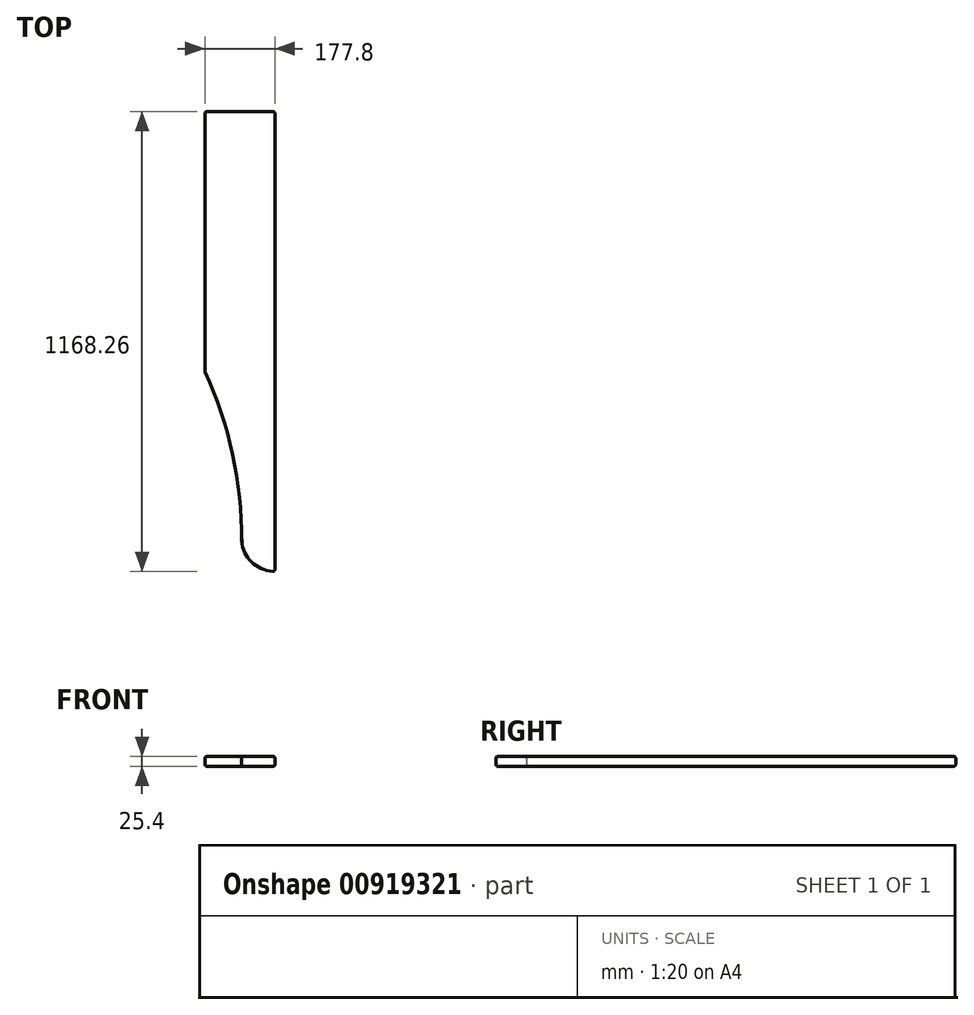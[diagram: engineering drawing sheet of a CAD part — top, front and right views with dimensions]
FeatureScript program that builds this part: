
annotation { "Feature Type Name" : "Feature", "Feature Type Description" : "" }
export const myFeature = defineFeature(function(context is Context, id is Id, definition is map)
    precondition{}
    {
        {
            var Q0;
            Q0=qCreatedBy(makeId("Top.planeOp"),FACE);
            var sketch = newSketch(context, id + "F0", { "sketchPlane" : qUnion([Q0])});
            skLineSegment(sketch, "E0.top", {"start": v(88.9, 584.2) * mm, "end": v(-88.9, 584.2) * mm});
            skLineSegment(sketch, "E0.left", {"start": v(88.9, -584.2) * mm, "end": v(88.9, 584.2) * mm});
            skPoint(sketch, "E0.middle", {"position": v(0, 0) * mm});
            skPoint(sketch, "E0.bottom.end.orphan", {"position": v(-88.9, -584.2) * mm});
            skLineSegment(sketch, "E1", {"start": v(-88.9, -76.2) * mm, "end": v(-88.9, 584.2) * mm});
            skArc(sketch, "E2", {"start": v(3.73, -506.4) * mm, "mid": v(-18.71, -286.16) * mm, "end": v(-88.9, -76.2) * mm});
            skArc(sketch, "E3", {"start": v(3.73, -506.4) * mm, "mid": v(31.13, -561.92) * mm, "end": v(88.9, -584.2) * mm});
            skPoint(sketch, "E4.orphan", {"position": v(0, -584.2) * mm});
            skSolve(sketch);
        }
        {
            var Q0;
            Q0 = qSketchRegion(id + "F0", true);
            extrude(context, id + "F1", {"entities" : qUnion([Q0]), "depth" : 25.4 * mm, "offsetDistance" : 25.4 * mm});
        }
        {
            var Q0;
            Q0=makeQuery(id+"F1.opExtrude","CAP_EDGE",EDGE,{"disambiguationData":[OSD([sQuery(id+"F0.wireOp",EDGE,"E1")])],"isStart":true});
            var Q1;
            Q1=makeQuery(id+"F1.opExtrude","CAP_EDGE",EDGE,{"disambiguationData":[OSD([sQuery(id+"F0.wireOp",EDGE,"E0.left")])],"isStart":false});
            var Q2;
            Q2=makeQuery(id+"F1.opExtrude","CAP_EDGE",EDGE,{"disambiguationData":[OSD([sQuery(id+"F0.wireOp",EDGE,"E0.top")])],"isStart":true});
            var Q3;
            Q3=makeQuery(id+"F1.opExtrude","CAP_EDGE",EDGE,{"disambiguationData":[OSD([sQuery(id+"F0.wireOp",EDGE,"E2")])],"isStart":true});
            var Q4;
            Q4=makeQuery(id+"F1.opExtrude","CAP_EDGE",EDGE,{"disambiguationData":[OSD([sQuery(id+"F0.wireOp",EDGE,"E3")])],"isStart":true});
            var Q5;
            Q5=makeQuery(id+"F1.opExtrude","CAP_EDGE",EDGE,{"disambiguationData":[OSD([sQuery(id+"F0.wireOp",EDGE,"E0.left")])],"isStart":true});
            var Q6;
            Q6=makeQuery(id+"F1.opExtrude","CAP_EDGE",EDGE,{"disambiguationData":[OSD([sQuery(id+"F0.wireOp",EDGE,"E3")])],"isStart":false});
            var Q7;
            Q7=makeQuery(id+"F1.opExtrude","SWEPT_EDGE",EDGE,{"disambiguationData":[OSD([sQuery(id+"F0.wireOp",EDGE,"E0.left"),sQuery(id+"F0.wireOp",EDGE,"E3")])]});
            var Q8;
            Q8=makeQuery(id+"F1.opExtrude","CAP_EDGE",EDGE,{"disambiguationData":[OSD([sQuery(id+"F0.wireOp",EDGE,"E2")])],"isStart":false});
            var Q9;
            Q9=makeQuery(id+"F1.opExtrude","CAP_EDGE",EDGE,{"disambiguationData":[OSD([sQuery(id+"F0.wireOp",EDGE,"E1")])],"isStart":false});
            var Q10;
            Q10=makeQuery(id+"F1.opExtrude","CAP_EDGE",EDGE,{"disambiguationData":[OSD([sQuery(id+"F0.wireOp",EDGE,"E0.top")])],"isStart":false});
            var Q11;
            Q11=makeQuery(id+"F1.opExtrude","SWEPT_EDGE",EDGE,{"disambiguationData":[OSD([sQuery(id+"F0.wireOp",EDGE,"E0.top"),sQuery(id+"F0.wireOp",EDGE,"E1")])]});
            var Q12;
            Q12=makeQuery(id+"F1.opExtrude","SWEPT_EDGE",EDGE,{"disambiguationData":[OSD([sQuery(id+"F0.wireOp",EDGE,"E1"),sQuery(id+"F0.wireOp",EDGE,"E2")])]});
            var Q13;
            Q13=makeQuery(id+"F1.opExtrude","SWEPT_EDGE",EDGE,{"disambiguationData":[OSD([sQuery(id+"F0.wireOp",EDGE,"E0.top"),sQuery(id+"F0.wireOp",EDGE,"E0.left")])]});
            fillet(context, id + "F2", {"entities" : qUnion([Q0, Q1, Q2, Q3, Q4, Q5, Q6, Q7, Q8, Q9, Q10, Q11, Q12, Q13]), "radius" : 5.08 * mm, "tangentPropagation" : true, "allowEdgeOverflow" : false});
        }
    });
